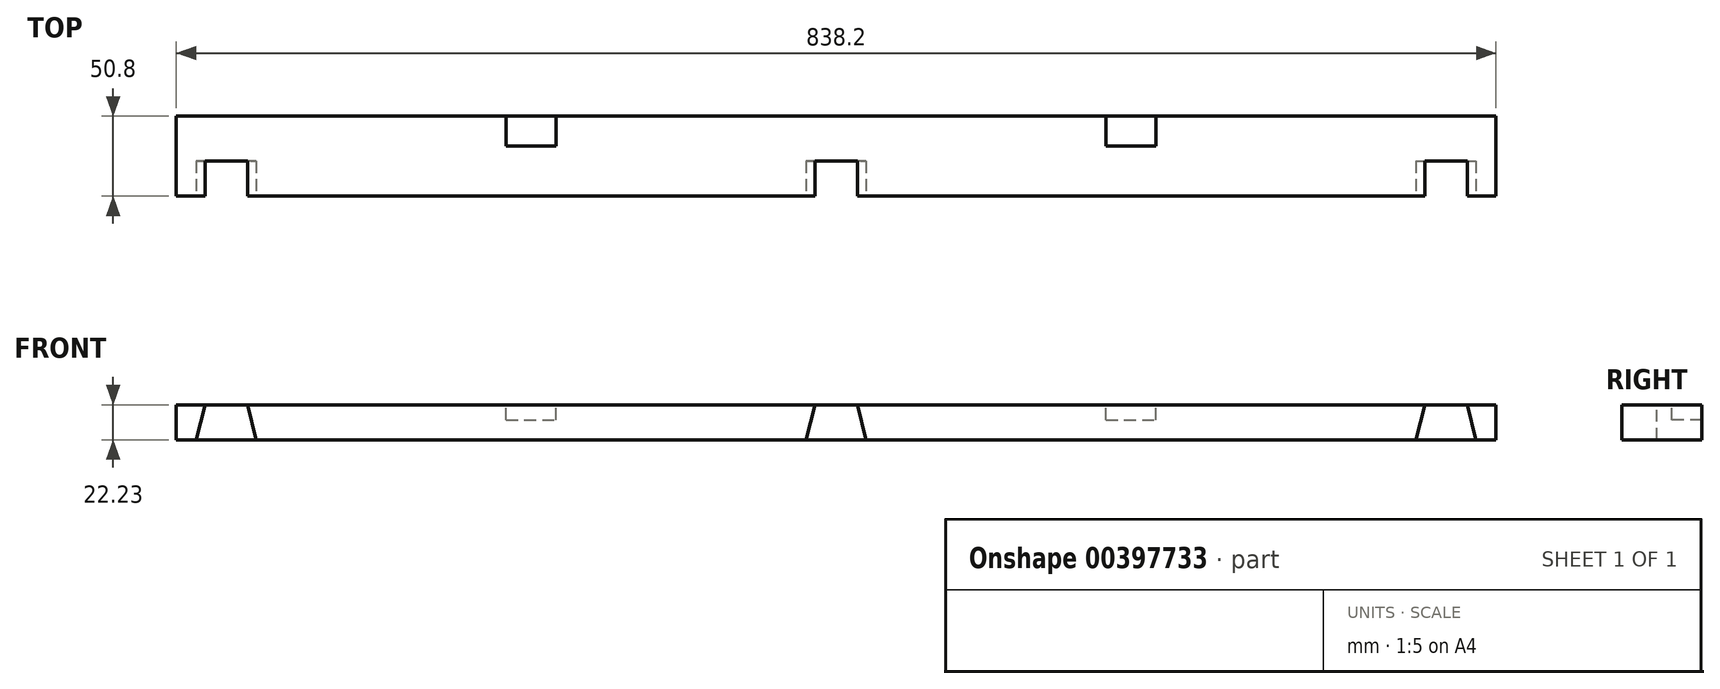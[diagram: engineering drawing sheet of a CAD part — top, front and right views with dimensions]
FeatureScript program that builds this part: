
annotation { "Feature Type Name" : "Feature", "Feature Type Description" : "" }
export const myFeature = defineFeature(function(context is Context, id is Id, definition is map)
    precondition{}
    {
        {
            var Q0;
            Q0=qCreatedBy(makeId("Front.planeOp"),FACE);
            var sketch = newSketch(context, id + "F0", { "sketchPlane" : qUnion([Q0])});
            skLineSegment(sketch, "E0.bottom", {"start": v(0, 0) * mm, "end": v(838.2, 0) * mm});
            skLineSegment(sketch, "E0.top", {"start": v(0, 22.23) * mm, "end": v(838.2, 22.23) * mm});
            skLineSegment(sketch, "E0.left", {"start": v(0, 0) * mm, "end": v(0, 22.23) * mm});
            skLineSegment(sketch, "E0.right", {"start": v(838.2, 0) * mm, "end": v(838.2, 22.23) * mm});
            skSolve(sketch);
        }
        {
            var Q0;
            Q0=makeQuery(id+"F0.imprint","IMPRINT",FACE,{"disambiguationData":[TD([[makeQuery(id+"F0.imprint","IMPRINT",EDGE,{"derivedFrom":sQuery(id+"F0.wireOp",EDGE,"E0.bottom")}),1.0]])]});
            extrude(context, id + "F1", {"entities" : qUnion([Q0]), "depth" : 50.8 * mm});
        }
        {
            var Q0;
            Q0=makeQuery(id+"F1.opExtrude","CAP_FACE",FACE,{"disambiguationData":[OSD([sQuery(id+"F0.wireOp",EDGE,"E0.bottom"),sQuery(id+"F0.wireOp",EDGE,"E0.top"),sQuery(id+"F0.wireOp",EDGE,"E0.left"),sQuery(id+"F0.wireOp",EDGE,"E0.right")])],"isStart":false});
            var sketch = newSketch(context, id + "F2", { "sketchPlane" : qUnion([Q0])});
            skLineSegment(sketch, "E1", {"start": v(400.05, 0) * mm, "end": v(438.15, 0) * mm});
            skLineSegment(sketch, "E2", {"start": v(438.15, 0) * mm, "end": v(432.6, 22.23) * mm});
            skLineSegment(sketch, "E3", {"start": v(432.6, 22.23) * mm, "end": v(405.6, 22.23) * mm});
            skLineSegment(sketch, "E4", {"start": v(405.6, 22.23) * mm, "end": v(400.05, 0) * mm});
            skLineSegment(sketch, "E5", {"start": v(438.15, 0) * mm, "end": v(438.15, 22.23) * mm, "construction": true});
            skLineSegment(sketch, "E6", {"start": v(438.15, 22.23) * mm, "end": v(432.6, 22.23) * mm, "construction": true});
            skLineSegment(sketch, "E7", {"start": v(400.05, 0) * mm, "end": v(400.05, 22.23) * mm, "construction": true});
            skLineSegment(sketch, "E8", {"start": v(400.05, 22.23) * mm, "end": v(405.6, 22.23) * mm, "construction": true});
            skPoint(sketch, "E9", {"position": v(419.1, 0) * mm});
            skLineSegment(sketch, "E10", {"start": v(18.24, 22.23) * mm, "end": v(12.7, 0) * mm});
            skLineSegment(sketch, "E11", {"start": v(12.7, 0) * mm, "end": v(50.8, 0) * mm});
            skLineSegment(sketch, "E12", {"start": v(50.8, 0) * mm, "end": v(45.26, 22.23) * mm});
            skLineSegment(sketch, "E13", {"start": v(45.26, 22.23) * mm, "end": v(18.24, 22.23) * mm});
            skLineSegment(sketch, "E14", {"start": v(819.96, 22.23) * mm, "end": v(825.5, 0) * mm});
            skLineSegment(sketch, "E15", {"start": v(825.5, 0) * mm, "end": v(787.4, 0) * mm});
            skLineSegment(sketch, "E16", {"start": v(787.4, 0) * mm, "end": v(792.94, 22.23) * mm});
            skLineSegment(sketch, "E17", {"start": v(792.94, 22.23) * mm, "end": v(819.96, 22.23) * mm});
            skSolve(sketch);
        }
        {
            var Q0;
            Q0=makeQuery(id+"F2.imprint","IMPRINT",FACE,{"disambiguationData":[TD([[makeQuery(id+"F2.imprint","IMPRINT",EDGE,{"derivedFrom":sQuery(id+"F2.wireOp",EDGE,"E1")}),1.0]])]});
            var Q1;
            Q1=makeQuery(id+"F2.imprint","IMPRINT",FACE,{"disambiguationData":[TD([[makeQuery(id+"F2.imprint","IMPRINT",EDGE,{"derivedFrom":sQuery(id+"F2.wireOp",EDGE,"E14")}),-1.0]])]});
            var Q2;
            Q2=makeQuery(id+"F2.imprint","IMPRINT",FACE,{"disambiguationData":[TD([[makeQuery(id+"F2.imprint","IMPRINT",EDGE,{"derivedFrom":sQuery(id+"F2.wireOp",EDGE,"E10")}),1.0]])]});
            extrude(context, id + "F3", {"entities" : qUnion([Q0, Q1, Q2]), "operationType" : NewBodyOperationType.REMOVE, "oppositeDirection" : true, "depth" : 22.22 * mm});
        }
        {
            var Q0;
            Q0=makeQuery(id+"F1.opExtrude","SWEPT_FACE",FACE,{"disambiguationData":[OSD([sQuery(id+"F0.wireOp",EDGE,"E0.top")])]});
            var sketch = newSketch(context, id + "F4", { "sketchPlane" : qUnion([Q0])});
            skLineSegment(sketch, "E18.bottom", {"start": v(209.55, 0) * mm, "end": v(241.3, 0) * mm});
            skLineSegment(sketch, "E18.top", {"start": v(209.55, -19.05) * mm, "end": v(241.3, -19.05) * mm});
            skLineSegment(sketch, "E18.left", {"start": v(209.55, 0) * mm, "end": v(209.55, -19.05) * mm});
            skLineSegment(sketch, "E18.right", {"start": v(241.3, 0) * mm, "end": v(241.3, -19.05) * mm});
            skLineSegment(sketch, "E19", {"start": v(50.8, 0) * mm, "end": v(50.8, -50.8) * mm, "construction": true});
            skLineSegment(sketch, "E20", {"start": v(400.05, 0) * mm, "end": v(400.05, -50.8) * mm, "construction": true});
            skLineSegment(sketch, "E21.bottom", {"start": v(590.55, 0) * mm, "end": v(622.3, 0) * mm});
            skLineSegment(sketch, "E21.top", {"start": v(590.55, -19.05) * mm, "end": v(622.3, -19.05) * mm});
            skLineSegment(sketch, "E21.left", {"start": v(590.55, 0) * mm, "end": v(590.55, -19.05) * mm});
            skLineSegment(sketch, "E21.right", {"start": v(622.3, 0) * mm, "end": v(622.3, -19.05) * mm});
            skSolve(sketch);
        }
        {
            var Q0;
            Q0=makeQuery(id+"F4.imprint","IMPRINT",FACE,{"disambiguationData":[TD([[makeQuery(id+"F4.imprint","IMPRINT",EDGE,{"derivedFrom":sQuery(id+"F4.wireOp",EDGE,"E18.bottom")}),-1.0]])]});
            var Q1;
            Q1=makeQuery(id+"F4.imprint","IMPRINT",FACE,{"disambiguationData":[TD([[makeQuery(id+"F4.imprint","IMPRINT",EDGE,{"derivedFrom":sQuery(id+"F4.wireOp",EDGE,"E21.bottom")}),-1.0]])]});
            extrude(context, id + "F5", {"entities" : qUnion([Q0, Q1]), "operationType" : NewBodyOperationType.REMOVE, "oppositeDirection" : true, "depth" : 9.52 * mm});
        }
    });
